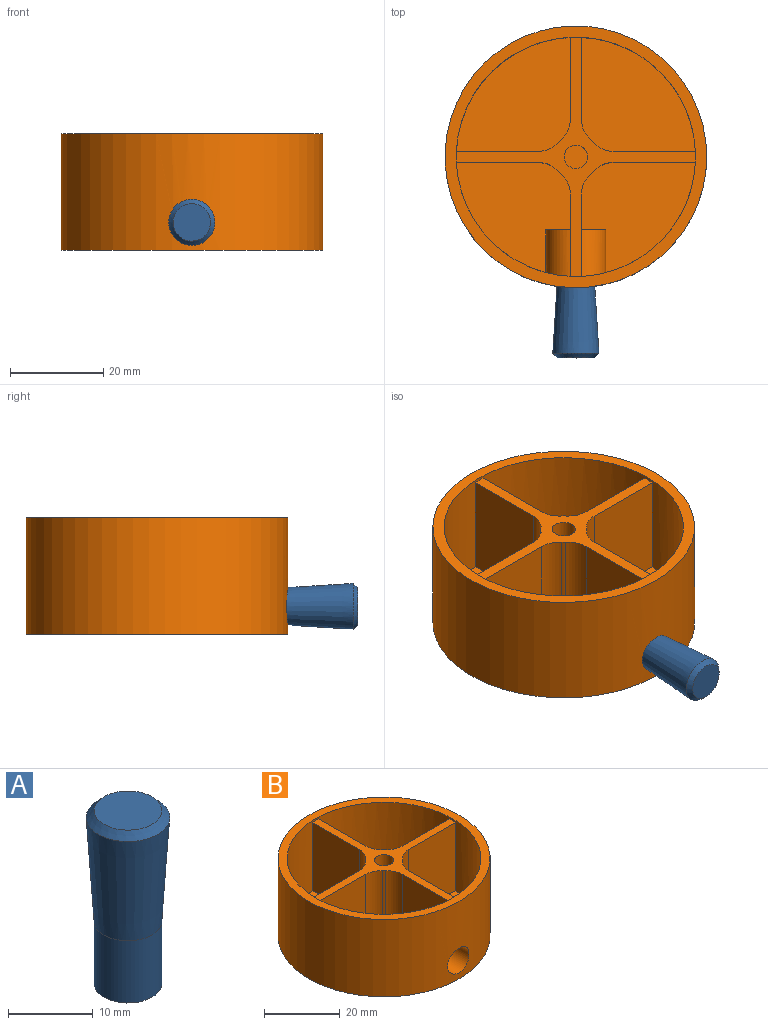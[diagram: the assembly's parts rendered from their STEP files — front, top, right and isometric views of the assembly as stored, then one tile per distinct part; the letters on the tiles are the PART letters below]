
ASSEMBLY  parts=2 mates=1
PART A: 5 faces, bbox 9.9x9.9x25 mm
  f0: plane 8x8mm, normal (0,0,1), area 50.3mm2, adj f4
  f1: cone r=5mm half-angle=3.6deg, axis (0,0,1), area 422.1mm2, adj f2,f4
  f2: cylinder r=4mm len=9mm, axis (0,0,-1), area 226.2mm2, adj f1,f3
  f3: plane 8x8mm, normal (0,0,-1), area 50.3mm2, adj f2
  f4: cone r=4.94mm half-angle=43.2deg, axis (0,0,-1), area 38.5mm2, adj f0,f1
PART B: 37 faces, bbox 56x56x25 mm
  f0: cylinder r=6.4mm len=9.97mm, axis (0,-1,0), area 119.9mm2, adj f3,f5,f13,f17
  f1: plane 24.37x24.37mm, normal (0,0,1), area 443.4mm2, adj f5,f14,f24,f25,f35,f36
  f2: plane 24.37x24.37mm, normal (0,0,1), area 443.4mm2, adj f5,f21,f22,f23,f33,f34
  f3: plane 24.37x23.85mm, normal (0,0,1), area 403.4mm2, adj f0,f5,f13,f15,f16,f17,f29,f30
  f4: plane 9.89x5.2mm, normal (0,1,0), area 42mm2, adj f11,f12,f18
  f5: cylinder r=25.6mm len=51.2mm, axis (0,0,1), area 3339.1mm2, adj f0,f1,f2,f3,f6,f11,f12,f14
  f6: plane 56x56mm, normal (0,0,1), area 404.1mm2, adj f5,f10
  f7: plane 56x56mm, normal (0,0,-1), area 2463mm2, adj f10
  f8: cylinder r=4mm len=10mm, axis (0,-1,0), area 247.7mm2, adj f9,f10
  f9: plane 8x8mm, normal (0,-1,0), area 50.3mm2, adj f8
  f10: cylinder r=28mm len=56mm, axis (0,0,1), area 4347.9mm2, adj f6,f7,f8
  f11: plane 24.37x23.85mm, normal (0,0,1), area 403.4mm2, adj f4,f5,f12,f18,f19,f20,f31,f32
  f12: cylinder r=6.4mm len=9.97mm, axis (0,-1,0), area 119.9mm2, adj f4,f5,f11,f18
  f13: plane 9.89x5.2mm, normal (0,1,0), area 42mm2, adj f0,f3,f17
  f14: plane 22x17.62mm, normal (0,1,0), area 387.6mm2, adj f1,f5,f27,f36
  f15: plane 22x17.62mm, normal (0,-1,0), area 387.6mm2, adj f3,f5,f27,f29
  f16: cylinder r=4.9mm len=22mm, axis (0,0,-1), area 18.4mm2, adj f3,f27,f29,f30
  f17: plane 22x17.62mm, normal (-1,0,0), area 289mm2, adj f0,f3,f5,f13,f27,f30
  f18: plane 22x17.62mm, normal (1,0,0), area 289mm2, adj f4,f5,f11,f12,f27,f31
  f19: cylinder r=4.9mm len=22mm, axis (0,0,-1), area 18.4mm2, adj f11,f27,f31,f32
  f20: plane 22x17.62mm, normal (0,-1,0), area 387.6mm2, adj f5,f11,f27,f32
  f21: plane 22x17.62mm, normal (0,1,0), area 387.6mm2, adj f2,f5,f27,f33
  f22: cylinder r=4.9mm len=22mm, axis (0,0,-1), area 18.4mm2, adj f2,f27,f33,f34
  f23: plane 22x17.62mm, normal (1,0,0), area 387.6mm2, adj f2,f5,f27,f34
  f24: plane 22x17.62mm, normal (-1,0,0), area 387.6mm2, adj f1,f5,f27,f35
  f25: cylinder r=4.9mm len=22mm, axis (0,0,-1), area 18.4mm2, adj f1,f27,f35,f36
  f26: cylinder r=2.5mm len=22mm, axis (0,0,-1), area 345.6mm2, adj f27,f28
  f27: plane 51.2x51.2mm, normal (0,0,1), area 265.7mm2, adj f5,f14,f15,f16,f17,f18,f19,f20
  f28: plane 5x5mm, normal (0,0,1), area 19.6mm2, adj f26
  f29: cylinder r=5.5mm len=22mm, axis (0,0,-1), area 105.4mm2, adj f3,f15,f16,f27
  f30: cylinder r=5.5mm len=22mm, axis (0,0,-1), area 105.4mm2, adj f3,f16,f17,f27
  f31: cylinder r=5.5mm len=22mm, axis (0,0,-1), area 105.4mm2, adj f11,f18,f19,f27
  f32: cylinder r=5.5mm len=22mm, axis (0,0,-1), area 105.4mm2, adj f11,f19,f20,f27
  f33: cylinder r=5.5mm len=22mm, axis (0,0,-1), area 105.4mm2, adj f2,f21,f22,f27
  f34: cylinder r=5.5mm len=22mm, axis (0,0,-1), area 105.4mm2, adj f2,f22,f23,f27
  f35: cylinder r=5.5mm len=22mm, axis (0,0,-1), area 105.4mm2, adj f1,f24,f25,f27
  f36: cylinder r=5.5mm len=22mm, axis (0,0,-1), area 105.4mm2, adj f1,f14,f25,f27
PLACE A rot(axis=(1,0,0),90deg) t=(0,-43,6)mm
PLACE B at identity
MATE fastened A.f1 <-> B.f0  axis (0,1,0) through (0,-18,6)mm
